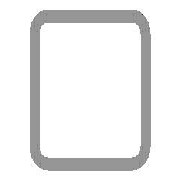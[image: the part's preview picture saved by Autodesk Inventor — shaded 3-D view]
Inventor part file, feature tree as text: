
AUTODESK INVENTOR PART (.ipt)
format: ipt  version: 2022 (Build 260153000, 153)  size: 249,344 bytes
history: native  units: mm (DEFAULTED — no unit token found)
features: other x7, sketch x3, surface_op x2, plane x1
ambient origin geometry x8: Origin, YZ Plane, XZ Plane, XY Plane, X Axis, Y Axis, Z Axis, Center Point
bodies: Solid1 (feature_tree), Body (feature_tree), Solid3 (feature_tree)
feature tree (13):
  parser-record x1  (decoder bookkeeping rows leaked as tree rows — omitted from the tree; the rows remain in map.json)
  other  "Driven Length"
  other  "Start Plane"
  other  "End Plane"
  sketch  "Sketch"  dims[d7=8.0mm d9=40.0mm d11=40.0mm d12=4.0mm d13=-0.0mm d14=180.0mm d15=20.0mm d16=20.0mm d17=90.0deg d18=180.0mm d37=5.0mm d38=5.0mm d39=5.0mm d40=5.0mm d41=5.0mm d42=5.0mm d43=5.0mm d44=5.0mm d45=0.0mm d46=5.0mm d47=5.0mm d48=5.0mm d49=5.0mm d50=5.0mm d51=5.0mm d52=5.0mm d53=5.0mm d54=0.0mm]
  sketch  "Sketch3"  dims[d3=156.0mm]
  plane  "Work Plane3"
  sketch  "Sketch4"  dims[d4=0.0mm]
  other  "Srf5"
  other  "Srf6"
  other  "Srf4"
  surface_op  "Boundary Patch3"
  surface_op  "Boundary Patch4"
